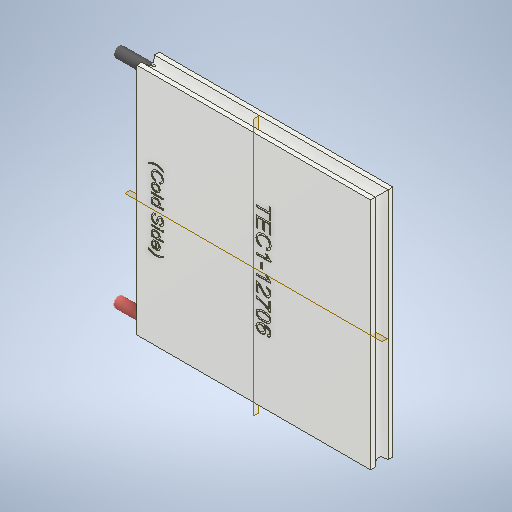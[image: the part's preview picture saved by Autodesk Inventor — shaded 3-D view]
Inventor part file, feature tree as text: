
AUTODESK INVENTOR PART (.ipt)
format: ipt  version: 2025.2 (Build 292293000, 293)  size: 891,392 bytes
history: native  units: in
note: dims shown in document units (in); Inventor stores cm internally (conversion verified against a paired STEP export)
features: other x3, plane x2
ambient origin geometry x8: Origin, YZ Plane, XZ Plane, XY Plane, X Axis, Y Axis, Z Axis, Center Point
bodies: Solid1 (feature_tree), Solid2 (feature_tree), Solid3 (feature_tree)
feature tree (5):
  plane  "Work Plane1"
  plane  "Work Plane2"
  other  "Positive"
  other  "Negative"
  other  "TEC Module"
